# Revit family: Power-ModularDevices-GEWISS-90AM-SWITCH_DISCONNECTOR_DC
name_source: partatom
category: Apparecchi elettrici
revit_build: Autodesk Revit 2016 (Build: 20161004_0715(x64)
units: mm (PartAtom-declared; Revit-internal decimal feet)

## family parameters
Condiviso = No
Host = Muro
Mantenere orientamento annotazione = Sì
Numero OmniClass = 23.80.50.00
Punto di calcolo locali = Sì
Quota connettore circolare = Usa diametro
Sempre verticale = Sì
Taglio con vuoti quando caricato = No
Tipo di parte = Normale
Titolo OmniClass = Terminals for Power Supply

## types (2) — shared parameters
Catalogue = POWER
Catalogue Range = 90 AM
Electrocod = 1422
IDF = 2d91bf4f-f6dc-4237-b79b-5006d058144e
IDT = 6c44909a-48af-40ca-be23-f546f73f6b37
Immagine tipo = GW96187.jpg
No. Chorus modules = 3,5
No. of modules EN 50022 = 3,5
Produttore = GEWISS S.p.A.
SEO = Disconnector
TIPO = GENERICO - 90AM SEZIONATORI DC : 4P
Technical sheet = https://www.gewiss.com
Type = Direct current
Type: = Direct current
URL = https://www.gewiss.com
Version file RFA = 18.0
sIMBOLO IN PIANTA = Sì

## per-type parameters (varying)
| type | Descrizione | EAN code | Modello | No. of poles | Number of poles | Rated current (In) | Rated current: | Rated voltage | Rated voltage DC |
| GW96187 - SWITCH DISCONNECTOR ROT 4P 32A 1000V DC | SWITCH DISCONNECTOR ROT 4P 32A 1000V DC | 8011564775480 | GW96187 | 4P | 4P | 32A | 32A | 1000Vdc | 1000V |
| GW96186 - SWITCH DISCONNECTOR ROT 2P 25A 600V DC | SWITCH DISCONNECTOR ROT 2P 25A 600V DC | 8011564775473 | GW96186 | 2P | 2P | 25A | 25A | 600Vdc | 600V |
